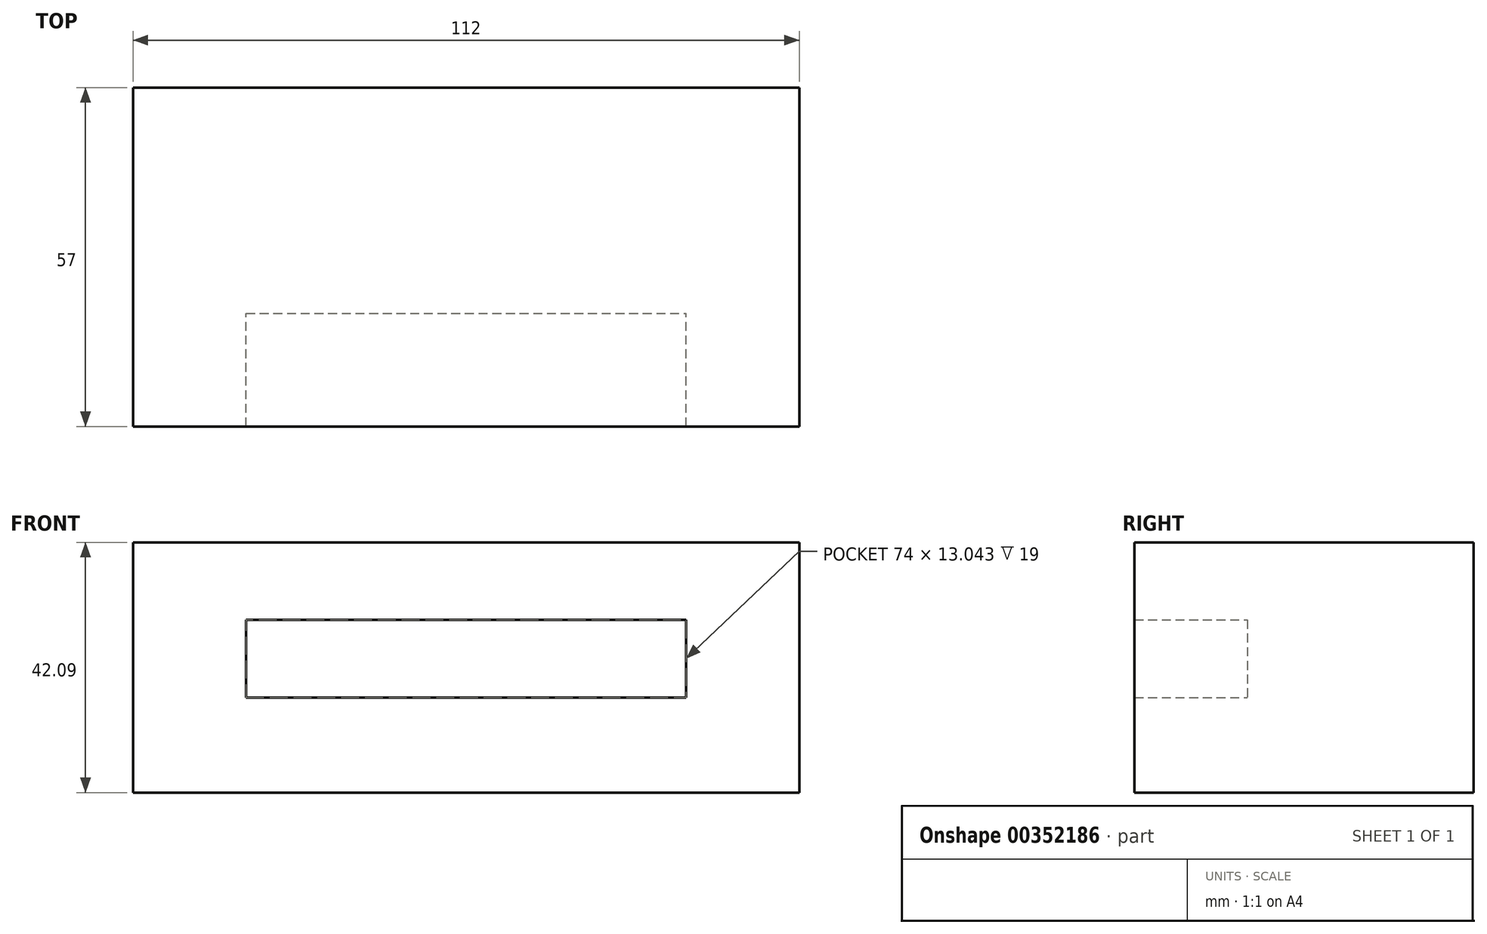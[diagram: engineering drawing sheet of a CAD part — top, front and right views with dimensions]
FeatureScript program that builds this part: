
annotation { "Feature Type Name" : "Feature", "Feature Type Description" : "" }
export const myFeature = defineFeature(function(context is Context, id is Id, definition is map)
    precondition{}
    {
        {
            var Q0;
            Q0=qCreatedBy(makeId("Front.planeOp"),FACE);
            var sketch = newSketch(context, id + "F0", { "sketchPlane" : qUnion([Q0])});
            skLineSegment(sketch, "E0.bottom", {"start": v(0, 0) * mm, "end": v(112, 0) * mm});
            skLineSegment(sketch, "E0.top", {"start": v(0, 42.09) * mm, "end": v(112, 42.09) * mm});
            skLineSegment(sketch, "E0.left", {"start": v(0, 0) * mm, "end": v(0, 42.09) * mm});
            skLineSegment(sketch, "E0.right", {"start": v(112, 0) * mm, "end": v(112, 42.09) * mm});
            skLineSegment(sketch, "E1.bottom", {"start": v(19, 42.09) * mm, "end": v(93, 42.09) * mm});
            skLineSegment(sketch, "E1.top", {"start": v(19, 16) * mm, "end": v(93, 16) * mm});
            skLineSegment(sketch, "E1.left", {"start": v(19, 42.09) * mm, "end": v(19, 16) * mm});
            skLineSegment(sketch, "E1.right", {"start": v(93, 42.09) * mm, "end": v(93, 16) * mm});
            skLineSegment(sketch, "E2", {"start": v(19, 29.04) * mm, "end": v(93, 29.04) * mm});
            skLineSegment(sketch, "E3", {"start": v(38, 29.04) * mm, "end": v(38, 16) * mm});
            skLineSegment(sketch, "E4", {"start": v(74, 29.04) * mm, "end": v(74, 16) * mm});
            skSolve(sketch);
        }
        {
            var Q0;
            Q0 = qSketchRegion(id + "F0", true);
            extrude(context, id + "F1", {"entities" : qUnion([Q0]), "depth" : 57 * mm});
        }
        {
            var Q0;
            {var subQ0=sQuery(id+"F0.wireOp",EDGE,"E3");Q0=makeQuery(id+"F0.imprint","IMPRINT",FACE,{"disambiguationData":[TD([[makeQuery(id+"F0.imprint","IMPRINT",EDGE,{"derivedFrom":subQ0}),1.0]])]});}
            var Q1;
            {var subQ3=sQuery(id+"F0.wireOp",EDGE,"E3");Q1=makeQuery(id+"F0.imprint","IMPRINT",FACE,{"disambiguationData":[TD([[makeQuery(id+"F0.imprint","IMPRINT",EDGE,{"derivedFrom":subQ3}),-1.0]])]});}
            var Q2;
            {var subQ3=sQuery(id+"F0.wireOp",EDGE,"E4");Q2=makeQuery(id+"F0.imprint","IMPRINT",FACE,{"disambiguationData":[TD([[makeQuery(id+"F0.imprint","IMPRINT",EDGE,{"derivedFrom":subQ3}),1.0]])]});}
            extrude(context, id + "F2", {"entities" : qUnion([Q0, Q1, Q2]), "operationType" : NewBodyOperationType.ADD, "depth" : 38 * mm});
        }
    });
